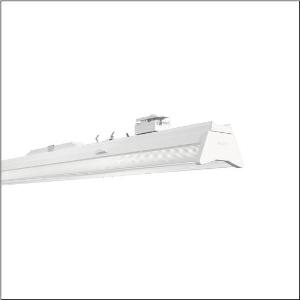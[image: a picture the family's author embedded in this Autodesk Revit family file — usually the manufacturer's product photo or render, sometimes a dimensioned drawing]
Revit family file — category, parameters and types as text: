
# Revit family: licross_r__21_performance_mo_52td16mn4a5g_2767
name_source: partatom
category: Lighting Fixtures
units: mm (PartAtom-declared; Revit-internal decimal feet)

## family parameters
Cut with Voids When Loaded = No
Host = Face
Light Source = No
Part Type = Normal
Room Calculation Point = No
Round Connector Dimension = Use Diameter
Shared = No

## types (1)
- --- (1 x LED, 10890 lm, 60.5 W, 4000K)
    Apparent Load = 61 VA
    CIE Flux Codes = 66 88 96 79 100
    Color Rendering = 80
    Color Temperature = 4000K
    Default Elevation = 1800 mm
    Description = Licross® 21 Performance MO, luminaire insert, of sheet steel, galvanised, coil coated, white, length: 1.500mm, width: 120mm, height: 123mm, LED rated luminous flux: 10.890lm, light colour: 840, SDCM (Standard Deviation of Colour Matching)MacAdam ≤ 3 SDCM (initial), control gear: ON/OFF Multilumen, with plug, 3-pole, with phase selection, mains connection: 220..240V, AC, 50/60Hz, rated input power: 61W, internal wiring halogen-free, primary light control with lens, of plastic, primary optical cover: cover, of PMMA, light emission: direct/indirect distribution, primary light characteristic: symmetric, protection rating (complete): IP54, insulation class (complete): insulation class I (protective earthing), certification: CE, ENEC, UKCA, protection symbol: D if used in an environment with non-conductive dust loads with corresponding accessories, impact resistance: IK06, permissible ambient temperature for indoor applications: -35..+45°C, corresponds to IFS (International Featured Standards) requirements for safety and quality in the food industry, reducing of maximum allowable ambient temperature of 5°C with ceiling mounting, LABS conformity tested according to VDMA 24364:2018-05, packaging unit: 1 piece
    Height = 114 mm
    Lamp = 1 x LED
    Lamp Light Flux = 10890 lm
    Lamp Power = 60.5 W
    Lamp count = 1
    Length = 1500 mm
    Luminous efficacy = 180 lm/W
    Manufacturer = Siteco
    ModVariant = No
    Model = 52TD16MN4A5G
    Mounting Place = Ceiling
    Mounting Type = Pendant
    Number of Poles = 1
    OnlyDefault = Yes
    Power Factor = 1
    Product Name = Licross® 21 Performance MO
    Product group = luminaire insert | ceiling pendant
    ProductGroupID = 901
    Protection Class = Protection class I
    Protection Degree = IP 54
    RLX_Detail_Level = 1
    RLX_Emergency_Light_Flux = 0 lm
    RLX_Emergency_Type = 0
    RLX_Emergency_Type_DB = No
    RlxData = <blob elided: 31921 chars, md5=90cac184>
    Socket = socket
    Standby Power = 0 W
    System Light Flux = 10890 lm
    System Power = 61 W
    Type Comments = factory setting: luminous flux: 100 % | (A | C | E) | 140 mA
    Type Image = l_1256138.jpg
    URL = http://relux.com
    VarID = @adj_113127
    Voltage = 0 V
    Weight = 0.00 kg
    Width = 120 mm

## geometry (parser evidence)
native form markers: Blend x4, Sweep x11
no freeform markers — native parametric forms only
